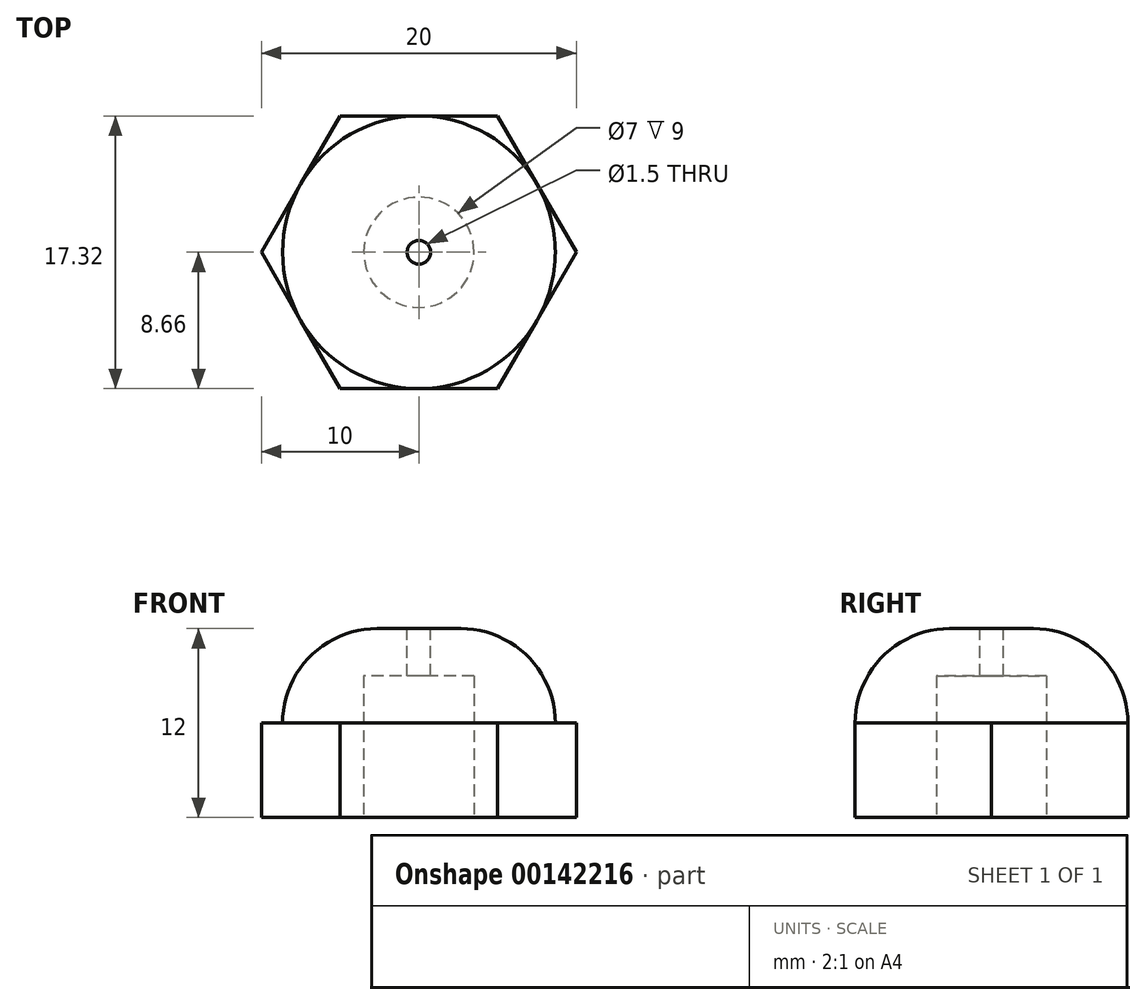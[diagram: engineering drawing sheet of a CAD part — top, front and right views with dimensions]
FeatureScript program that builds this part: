
annotation { "Feature Type Name" : "Feature", "Feature Type Description" : "" }
export const myFeature = defineFeature(function(context is Context, id is Id, definition is map)
    precondition{}
    {
        {
            var Q0;
            Q0=qCreatedBy(makeId("Top.planeOp"),FACE);
            var sketch = newSketch(context, id + "F0", { "sketchPlane" : qUnion([Q0])});
            skCircle(sketch, "E0", {"center": v(0, 0) * mm, "radius": 3.5 * mm});
            skLineSegment(sketch, "E1", {"start": v(-5, 8.66) * mm, "end": v(5, 8.66) * mm});
            skLineSegment(sketch, "E2", {"start": v(-5, 8.66) * mm, "end": v(-10, 0) * mm});
            skLineSegment(sketch, "E3", {"start": v(-10, 0) * mm, "end": v(-5, -8.66) * mm});
            skLineSegment(sketch, "E4", {"start": v(-5, -8.66) * mm, "end": v(5, -8.66) * mm});
            skLineSegment(sketch, "E5", {"start": v(5, -8.66) * mm, "end": v(10, 0) * mm});
            skLineSegment(sketch, "E6", {"start": v(5, 8.66) * mm, "end": v(10, 0) * mm});
            skLineSegment(sketch, "E7", {"start": v(-5, 8.66) * mm, "end": v(5, -8.66) * mm, "construction": true});
            skSolve(sketch);
        }
        {
            var Q0;
            Q0=qSketchRegion(id+"F0",true);
            extrude(context, id + "F1", {"entities" : qUnion([Q0]), "depth" : 6 * mm});
        }
        {
            var Q0;
            Q0=makeQuery(id+"F1.opExtrude","CAP_FACE",FACE,{"disambiguationData":[OSD([sQuery(id+"F0.wireOp",EDGE,"E0"),sQuery(id+"F0.wireOp",EDGE,"E1"),sQuery(id+"F0.wireOp",EDGE,"E2"),sQuery(id+"F0.wireOp",EDGE,"E3"),sQuery(id+"F0.wireOp",EDGE,"E4"),sQuery(id+"F0.wireOp",EDGE,"E5"),sQuery(id+"F0.wireOp",EDGE,"E6")])],"isStart":false});
            var sketch = newSketch(context, id + "F2", { "sketchPlane" : qUnion([Q0])});
            skCircle(sketch, "E8", {"center": v(0, 0) * mm, "radius": 8.66 * mm});
            skSolve(sketch);
        }
        {
            var Q0;
            Q0=qSketchRegion(id+"F2",true);
            extrude(context, id + "F3", {"entities" : qUnion([Q0]), "operationType" : NewBodyOperationType.ADD, "depth" : 6 * mm});
        }
        {
            var Q0;
            Q0=makeQuery(id+"F3.opExtrude","CAP_EDGE",EDGE,{"disambiguationData":[OSD([sQuery(id+"F2.wireOp",EDGE,"E8")])],"isStart":false});
            fillet(context, id + "F4", {"entities" : qUnion([Q0]), "radius" : 6 * mm, "tangentPropagation" : true, "allowEdgeOverflow" : false});
        }
        {
            var Q0;
            Q0=makeQuery(id+"F3.opExtrude","CAP_FACE",FACE,{"disambiguationData":[OSD([sQuery(id+"F2.wireOp",EDGE,"E8")])],"isStart":false});
            var sketch = newSketch(context, id + "F5", { "sketchPlane" : qUnion([Q0])});
            skCircle(sketch, "E9", {"center": v(0, 0) * mm, "radius": 0.75 * mm});
            skSolve(sketch);
        }
        {
            var Q0;
            Q0=makeQuery(id+"F3.opExtrude","CAP_FACE",FACE,{"disambiguationData":[OSD([sQuery(id+"F2.wireOp",EDGE,"E8")])],"isStart":true});
            extrude(context, id + "F6", {"entities" : qUnion([Q0]), "operationType" : NewBodyOperationType.REMOVE, "oppositeDirection" : true, "depth" : 3 * mm});
        }
        {
            var Q0;
            Q0=qSketchRegion(id+"F5",true);
            extrude(context, id + "F7", {"entities" : qUnion([Q0]), "operationType" : NewBodyOperationType.REMOVE, "endBound" : BoundingType.THROUGH_ALL, "oppositeDirection" : true, "depth" : 25 * mm});
        }
    });
